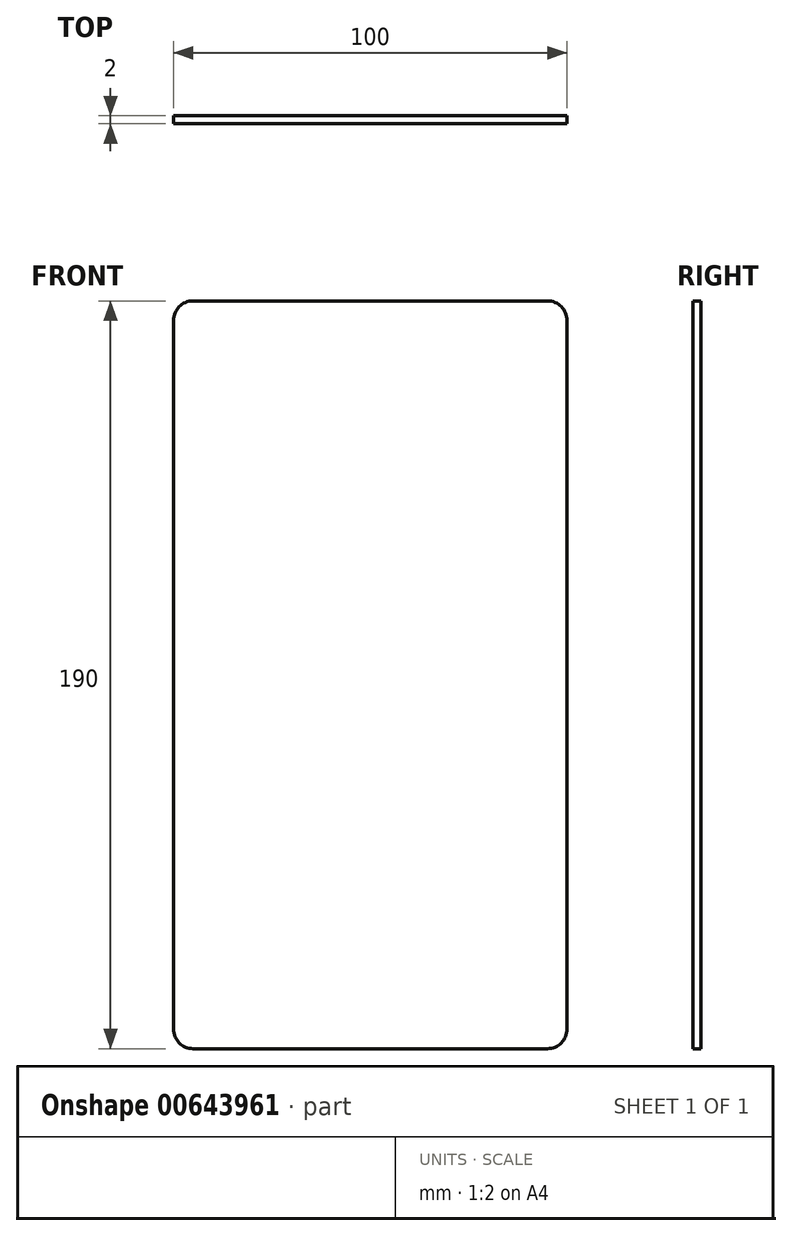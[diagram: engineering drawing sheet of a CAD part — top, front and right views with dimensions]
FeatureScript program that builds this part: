
annotation { "Feature Type Name" : "Feature", "Feature Type Description" : "" }
export const myFeature = defineFeature(function(context is Context, id is Id, definition is map)
    precondition{}
    {
        {
            var Q0;
            Q0=qCreatedBy(makeId("Front.planeOp"),FACE);
            var sketch = newSketch(context, id + "F0", { "sketchPlane" : qUnion([Q0])});
            skLineSegment(sketch, "E0.bottom", {"start": v(-5, 0) * mm, "end": v(-95, 0) * mm});
            skLineSegment(sketch, "E0.top", {"start": v(-5, 190) * mm, "end": v(-95, 190) * mm});
            skLineSegment(sketch, "E0.left", {"start": v(0, 5) * mm, "end": v(0, 185) * mm});
            skLineSegment(sketch, "E0.right", {"start": v(-100, 5) * mm, "end": v(-100, 185) * mm});
            skPoint(sketch, "E1.visualSharp", {"position": v(-100, 190) * mm});
            skArc(sketch, "E1.filletArc", {"start": v(-95, 190) * mm, "mid": v(-98.54, 188.54) * mm, "end": v(-100, 185) * mm});
            skPoint(sketch, "E2.visualSharp", {"position": v(0, 190) * mm});
            skArc(sketch, "E2.filletArc", {"start": v(0, 185) * mm, "mid": v(-1.46, 188.54) * mm, "end": v(-5, 190) * mm});
            skPoint(sketch, "E3.visualSharp", {"position": v(-100, 0) * mm});
            skArc(sketch, "E3.filletArc", {"start": v(-100, 5) * mm, "mid": v(-98.54, 1.46) * mm, "end": v(-95, 0) * mm});
            skPoint(sketch, "E4.visualSharp", {"position": v(0, 0) * mm});
            skArc(sketch, "E4.filletArc", {"start": v(-5, 0) * mm, "mid": v(-1.46, 1.46) * mm, "end": v(0, 5) * mm});
            skSolve(sketch);
        }
        {
            var Q0;
            Q0=makeQuery(id+"F0.imprint","IMPRINT",FACE,{"disambiguationData":[TD([[makeQuery(id+"F0.imprint","IMPRINT",EDGE,{"derivedFrom":sQuery(id+"F0.wireOp",EDGE,"E0.bottom")}),-1.0]])]});
            extrude(context, id + "F1", {"entities" : qUnion([Q0]), "depth" : 2 * mm, "offsetDistance" : 25 * mm});
        }
    });
